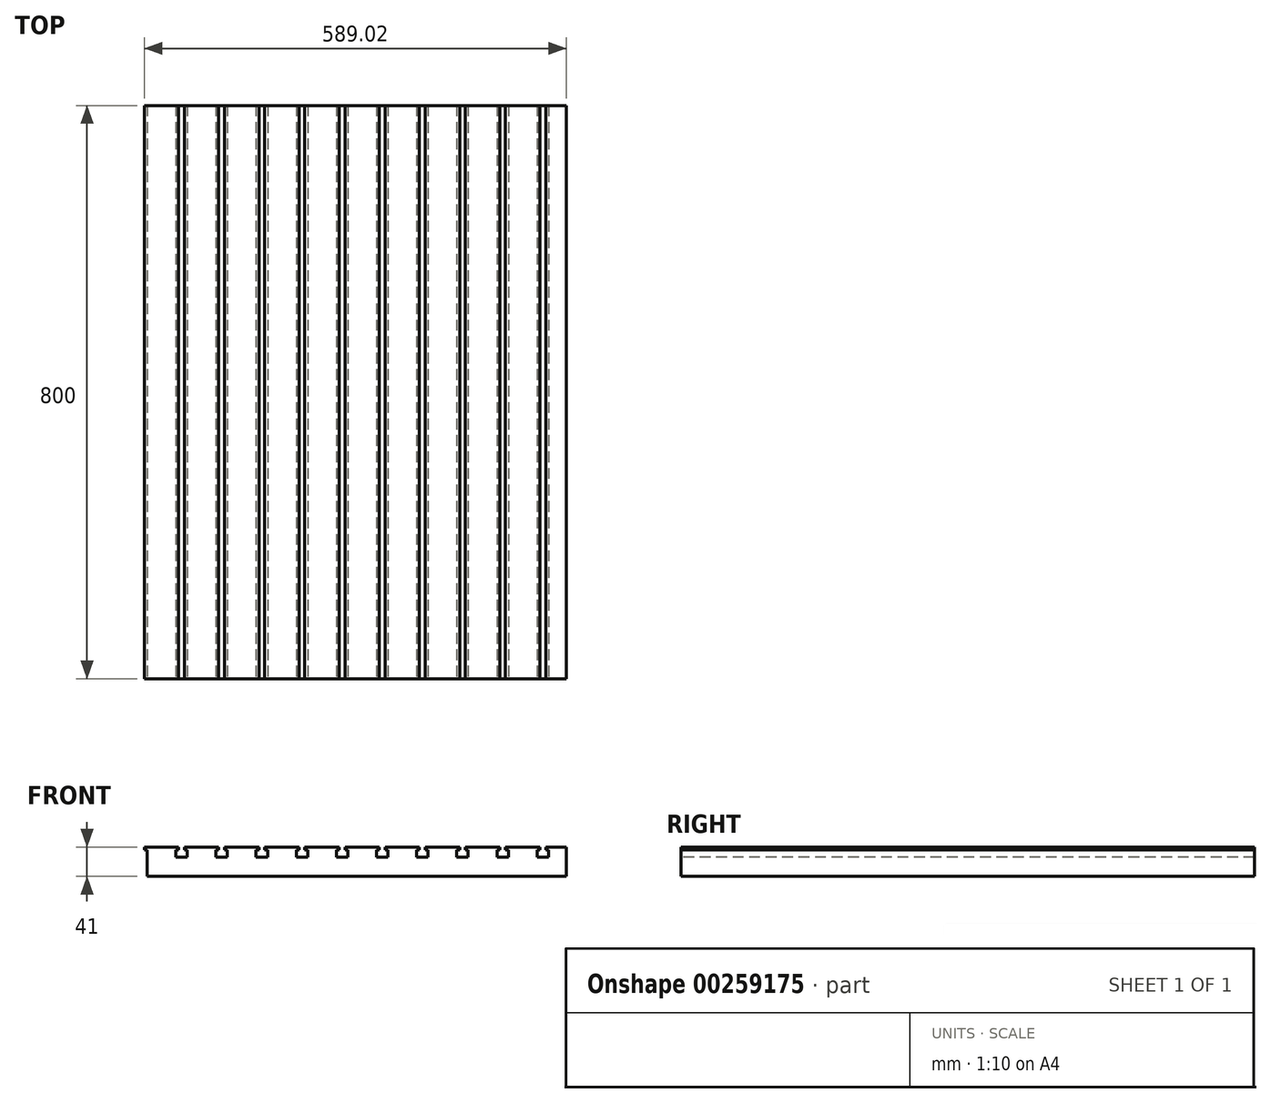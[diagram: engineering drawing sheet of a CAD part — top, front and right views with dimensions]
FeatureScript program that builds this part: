
annotation { "Feature Type Name" : "Feature", "Feature Type Description" : "" }
export const myFeature = defineFeature(function(context is Context, id is Id, definition is map)
    precondition{}
    {
        {
            var Q0;
            Q0=qCreatedBy(makeId("Top.planeOp"),FACE);
            var sketch = newSketch(context, id + "F0", { "sketchPlane" : qUnion([Q0])});
            skLineSegment(sketch, "E0.bottom", {"start": v(-545.89, 726.67) * mm, "end": v(39.11, 726.67) * mm});
            skLineSegment(sketch, "E0.top", {"start": v(-545.89, -73.33) * mm, "end": v(39.11, -73.33) * mm});
            skLineSegment(sketch, "E0.left", {"start": v(-545.89, 726.67) * mm, "end": v(-545.89, -73.33) * mm});
            skLineSegment(sketch, "E0.right", {"start": v(39.11, 726.67) * mm, "end": v(39.11, -73.33) * mm});
            skSolve(sketch);
        }
        {
            var Q0;
            Q0=makeQuery(id+"F0.imprint","IMPRINT",FACE,{"disambiguationData":[TD([[makeQuery(id+"F0.imprint","IMPRINT",EDGE,{"derivedFrom":sQuery(id+"F0.wireOp",EDGE,"E0.bottom")}),-1.0]])]});
            extrude(context, id + "F1", {"entities" : qUnion([Q0]), "depth" : 37 * mm});
        }
        {
            var Q0;
            Q0=makeQuery(id+"F1.opExtrude","CAP_FACE",FACE,{"disambiguationData":[OSD([sQuery(id+"F0.wireOp",EDGE,"E0.bottom"),sQuery(id+"F0.wireOp",EDGE,"E0.top"),sQuery(id+"F0.wireOp",EDGE,"E0.left"),sQuery(id+"F0.wireOp",EDGE,"E0.right")])],"isStart":false});
            var sketch = newSketch(context, id + "F2", { "sketchPlane" : qUnion([Q0])});
            skLineSegment(sketch, "E1.bottom", {"start": v(-505.89, 726.67) * mm, "end": v(-489.89, 726.67) * mm});
            skLineSegment(sketch, "E1.top", {"start": v(-505.89, -73.33) * mm, "end": v(-489.89, -73.33) * mm});
            skLineSegment(sketch, "E1.left", {"start": v(-505.89, 726.67) * mm, "end": v(-505.89, -73.33) * mm});
            skLineSegment(sketch, "E1.right", {"start": v(-489.89, 726.67) * mm, "end": v(-489.89, -73.33) * mm});
            skLineSegment(sketch, "E2.1.0.0", {"start": v(-449.89, 726.67) * mm, "end": v(-449.89, -73.33) * mm});
            skLineSegment(sketch, "E2.1.0.1", {"start": v(-433.89, 726.67) * mm, "end": v(-433.89, -73.33) * mm});
            skLineSegment(sketch, "E2.1.0.2", {"start": v(-449.89, 726.67) * mm, "end": v(-433.89, 726.67) * mm});
            skLineSegment(sketch, "E2.1.0.3", {"start": v(-449.89, -73.33) * mm, "end": v(-433.89, -73.33) * mm});
            skLineSegment(sketch, "E2.2.0.0", {"start": v(-393.89, 726.67) * mm, "end": v(-393.89, -73.33) * mm});
            skLineSegment(sketch, "E2.2.0.1", {"start": v(-377.89, 726.67) * mm, "end": v(-377.89, -73.33) * mm});
            skLineSegment(sketch, "E2.2.0.2", {"start": v(-393.89, 726.67) * mm, "end": v(-377.89, 726.67) * mm});
            skLineSegment(sketch, "E2.2.0.3", {"start": v(-393.89, -73.33) * mm, "end": v(-377.89, -73.33) * mm});
            skLineSegment(sketch, "E2.3.0.0", {"start": v(-337.89, 726.67) * mm, "end": v(-337.89, -73.33) * mm});
            skLineSegment(sketch, "E2.3.0.1", {"start": v(-321.89, 726.67) * mm, "end": v(-321.89, -73.33) * mm});
            skLineSegment(sketch, "E2.3.0.2", {"start": v(-337.89, 726.67) * mm, "end": v(-321.89, 726.67) * mm});
            skLineSegment(sketch, "E2.3.0.3", {"start": v(-337.89, -73.33) * mm, "end": v(-321.89, -73.33) * mm});
            skLineSegment(sketch, "E2.4.0.0", {"start": v(-281.89, 726.67) * mm, "end": v(-281.89, -73.33) * mm});
            skLineSegment(sketch, "E2.4.0.1", {"start": v(-265.89, 726.67) * mm, "end": v(-265.89, -73.33) * mm});
            skLineSegment(sketch, "E2.4.0.2", {"start": v(-281.89, 726.67) * mm, "end": v(-265.89, 726.67) * mm});
            skLineSegment(sketch, "E2.4.0.3", {"start": v(-281.89, -73.33) * mm, "end": v(-265.89, -73.33) * mm});
            skLineSegment(sketch, "E2.5.0.0", {"start": v(-225.89, 726.67) * mm, "end": v(-225.89, -73.33) * mm});
            skLineSegment(sketch, "E2.5.0.1", {"start": v(-209.89, 726.67) * mm, "end": v(-209.89, -73.33) * mm});
            skLineSegment(sketch, "E2.5.0.2", {"start": v(-225.89, 726.67) * mm, "end": v(-209.89, 726.67) * mm});
            skLineSegment(sketch, "E2.5.0.3", {"start": v(-225.89, -73.33) * mm, "end": v(-209.89, -73.33) * mm});
            skLineSegment(sketch, "E2.6.0.0", {"start": v(-169.89, 726.67) * mm, "end": v(-169.89, -73.33) * mm});
            skLineSegment(sketch, "E2.6.0.1", {"start": v(-153.89, 726.67) * mm, "end": v(-153.89, -73.33) * mm});
            skLineSegment(sketch, "E2.6.0.2", {"start": v(-169.89, 726.67) * mm, "end": v(-153.89, 726.67) * mm});
            skLineSegment(sketch, "E2.6.0.3", {"start": v(-169.89, -73.33) * mm, "end": v(-153.89, -73.33) * mm});
            skLineSegment(sketch, "E2.7.0.0", {"start": v(-113.89, 726.67) * mm, "end": v(-113.89, -73.33) * mm});
            skLineSegment(sketch, "E2.7.0.1", {"start": v(-97.89, 726.67) * mm, "end": v(-97.89, -73.33) * mm});
            skLineSegment(sketch, "E2.7.0.2", {"start": v(-113.89, 726.67) * mm, "end": v(-97.89, 726.67) * mm});
            skLineSegment(sketch, "E2.7.0.3", {"start": v(-113.89, -73.33) * mm, "end": v(-97.89, -73.33) * mm});
            skLineSegment(sketch, "E2.8.0.0", {"start": v(-57.89, 726.67) * mm, "end": v(-57.89, -73.33) * mm});
            skLineSegment(sketch, "E2.8.0.1", {"start": v(-41.89, 726.67) * mm, "end": v(-41.89, -73.33) * mm});
            skLineSegment(sketch, "E2.8.0.2", {"start": v(-57.89, 726.67) * mm, "end": v(-41.89, 726.67) * mm});
            skLineSegment(sketch, "E2.8.0.3", {"start": v(-57.89, -73.33) * mm, "end": v(-41.89, -73.33) * mm});
            skLineSegment(sketch, "E2.9.0.0", {"start": v(-1.89, 726.67) * mm, "end": v(-1.89, -73.33) * mm});
            skLineSegment(sketch, "E2.9.0.1", {"start": v(14.11, 726.67) * mm, "end": v(14.11, -73.33) * mm});
            skLineSegment(sketch, "E2.9.0.2", {"start": v(-1.89, 726.67) * mm, "end": v(14.11, 726.67) * mm});
            skLineSegment(sketch, "E2.9.0.3", {"start": v(-1.89, -73.33) * mm, "end": v(14.11, -73.33) * mm});
            skLineSegment(sketch, "E2.direction1", {"start": v(-505.89, -73.33) * mm, "end": v(-449.89, -73.33) * mm, "construction": true});
            skSolve(sketch);
        }
        {
            var Q0;
            Q0 = qSketchRegion(id + "F2", true);
            extrude(context, id + "F3", {"entities" : qUnion([Q0]), "operationType" : NewBodyOperationType.REMOVE, "oppositeDirection" : true, "depth" : 10 * mm});
        }
        {
            var Q0;
            {var subQ0=sQuery(id+"F0.wireOp",EDGE,"E0.bottom");var subQ1=sQuery(id+"F0.wireOp",EDGE,"E0.top");var subQ2=sQuery(id+"F0.wireOp",EDGE,"E0.left");Q0=makeQuery(id+"F3.boolean.opBoolean","SPLIT",FACE,{"disambiguationData":[TD([makeQuery(id+"F1.opExtrude","SWEPT_FACE",FACE,{"disambiguationData":[OSD([subQ2])]})])],"derivedFrom":makeQuery(id+"F1.opExtrude","CAP_FACE",FACE,{"disambiguationData":[OSD([subQ0,subQ1,subQ2,sQuery(id+"F0.wireOp",EDGE,"E0.right")])],"isStart":false})});}
            var sketch = newSketch(context, id + "F4", { "sketchPlane" : qUnion([Q0])});
            skLineSegment(sketch, "E3.bottom", {"start": v(-549.89, -73.33) * mm, "end": v(-501.89, -73.33) * mm});
            skLineSegment(sketch, "E3.top", {"start": v(-549.89, 726.67) * mm, "end": v(-501.89, 726.67) * mm});
            skLineSegment(sketch, "E3.left", {"start": v(-549.89, -73.33) * mm, "end": v(-549.89, 726.67) * mm});
            skLineSegment(sketch, "E3.right", {"start": v(-501.89, -73.33) * mm, "end": v(-501.89, 726.67) * mm});
            skLineSegment(sketch, "E4.1.0.0", {"start": v(-445.89, -73.33) * mm, "end": v(-445.89, 726.67) * mm});
            skLineSegment(sketch, "E4.1.0.1", {"start": v(-493.89, -73.33) * mm, "end": v(-493.89, 726.67) * mm});
            skLineSegment(sketch, "E4.1.0.2", {"start": v(-493.89, -73.33) * mm, "end": v(-445.89, -73.33) * mm});
            skLineSegment(sketch, "E4.1.0.3", {"start": v(-493.89, 726.67) * mm, "end": v(-445.89, 726.67) * mm});
            skLineSegment(sketch, "E4.2.0.0", {"start": v(-389.89, -73.33) * mm, "end": v(-389.89, 726.67) * mm});
            skLineSegment(sketch, "E4.2.0.1", {"start": v(-437.89, -73.33) * mm, "end": v(-437.89, 726.67) * mm});
            skLineSegment(sketch, "E4.2.0.2", {"start": v(-437.89, -73.33) * mm, "end": v(-389.89, -73.33) * mm});
            skLineSegment(sketch, "E4.2.0.3", {"start": v(-437.89, 726.67) * mm, "end": v(-389.89, 726.67) * mm});
            skLineSegment(sketch, "E4.3.0.0", {"start": v(-333.89, -73.33) * mm, "end": v(-333.89, 726.67) * mm});
            skLineSegment(sketch, "E4.3.0.1", {"start": v(-381.89, -73.33) * mm, "end": v(-381.89, 726.67) * mm});
            skLineSegment(sketch, "E4.3.0.2", {"start": v(-381.89, -73.33) * mm, "end": v(-333.89, -73.33) * mm});
            skLineSegment(sketch, "E4.3.0.3", {"start": v(-381.89, 726.67) * mm, "end": v(-333.89, 726.67) * mm});
            skLineSegment(sketch, "E4.4.0.0", {"start": v(-277.89, -73.33) * mm, "end": v(-277.89, 726.67) * mm});
            skLineSegment(sketch, "E4.4.0.1", {"start": v(-325.89, -73.33) * mm, "end": v(-325.89, 726.67) * mm});
            skLineSegment(sketch, "E4.4.0.2", {"start": v(-325.89, -73.33) * mm, "end": v(-277.89, -73.33) * mm});
            skLineSegment(sketch, "E4.4.0.3", {"start": v(-325.89, 726.67) * mm, "end": v(-277.89, 726.67) * mm});
            skLineSegment(sketch, "E4.5.0.0", {"start": v(-221.89, -73.33) * mm, "end": v(-221.89, 726.67) * mm});
            skLineSegment(sketch, "E4.5.0.1", {"start": v(-269.89, -73.33) * mm, "end": v(-269.89, 726.67) * mm});
            skLineSegment(sketch, "E4.5.0.2", {"start": v(-269.89, -73.33) * mm, "end": v(-221.89, -73.33) * mm});
            skLineSegment(sketch, "E4.5.0.3", {"start": v(-269.89, 726.67) * mm, "end": v(-221.89, 726.67) * mm});
            skLineSegment(sketch, "E4.6.0.0", {"start": v(-165.89, -73.33) * mm, "end": v(-165.89, 726.67) * mm});
            skLineSegment(sketch, "E4.6.0.1", {"start": v(-213.89, -73.33) * mm, "end": v(-213.89, 726.67) * mm});
            skLineSegment(sketch, "E4.6.0.2", {"start": v(-213.89, -73.33) * mm, "end": v(-165.89, -73.33) * mm});
            skLineSegment(sketch, "E4.6.0.3", {"start": v(-213.89, 726.67) * mm, "end": v(-165.89, 726.67) * mm});
            skLineSegment(sketch, "E4.7.0.0", {"start": v(-109.89, -73.33) * mm, "end": v(-109.89, 726.67) * mm});
            skLineSegment(sketch, "E4.7.0.1", {"start": v(-157.89, -73.33) * mm, "end": v(-157.89, 726.67) * mm});
            skLineSegment(sketch, "E4.7.0.2", {"start": v(-157.89, -73.33) * mm, "end": v(-109.89, -73.33) * mm});
            skLineSegment(sketch, "E4.7.0.3", {"start": v(-157.89, 726.67) * mm, "end": v(-109.89, 726.67) * mm});
            skLineSegment(sketch, "E4.8.0.0", {"start": v(-53.89, -73.33) * mm, "end": v(-53.89, 726.67) * mm});
            skLineSegment(sketch, "E4.8.0.1", {"start": v(-101.89, -73.33) * mm, "end": v(-101.89, 726.67) * mm});
            skLineSegment(sketch, "E4.8.0.2", {"start": v(-101.89, -73.33) * mm, "end": v(-53.89, -73.33) * mm});
            skLineSegment(sketch, "E4.8.0.3", {"start": v(-101.89, 726.67) * mm, "end": v(-53.89, 726.67) * mm});
            skLineSegment(sketch, "E4.9.0.0", {"start": v(2.11, -73.33) * mm, "end": v(2.11, 726.67) * mm});
            skLineSegment(sketch, "E4.9.0.1", {"start": v(-45.89, -73.33) * mm, "end": v(-45.89, 726.67) * mm});
            skLineSegment(sketch, "E4.9.0.2", {"start": v(-45.89, -73.33) * mm, "end": v(2.11, -73.33) * mm});
            skLineSegment(sketch, "E4.9.0.3", {"start": v(-45.89, 726.67) * mm, "end": v(2.11, 726.67) * mm});
            skLineSegment(sketch, "E4.direction1", {"start": v(-549.89, -73.33) * mm, "end": v(-493.89, -73.33) * mm, "construction": true});
            skLineSegment(sketch, "E5.bottom", {"start": v(39.13, 726.67) * mm, "end": v(10.11, 726.67) * mm});
            skLineSegment(sketch, "E5.top", {"start": v(39.13, -73.33) * mm, "end": v(10.11, -73.33) * mm});
            skLineSegment(sketch, "E5.left", {"start": v(39.13, 726.67) * mm, "end": v(39.13, -73.33) * mm});
            skLineSegment(sketch, "E5.right", {"start": v(10.11, 726.67) * mm, "end": v(10.11, -73.33) * mm});
            skSolve(sketch);
        }
        {
            var Q0;
            Q0 = qSketchRegion(id + "F4", true);
            extrude(context, id + "F5", {"entities" : qUnion([Q0]), "operationType" : NewBodyOperationType.ADD, "depth" : 4 * mm});
        }
    });
